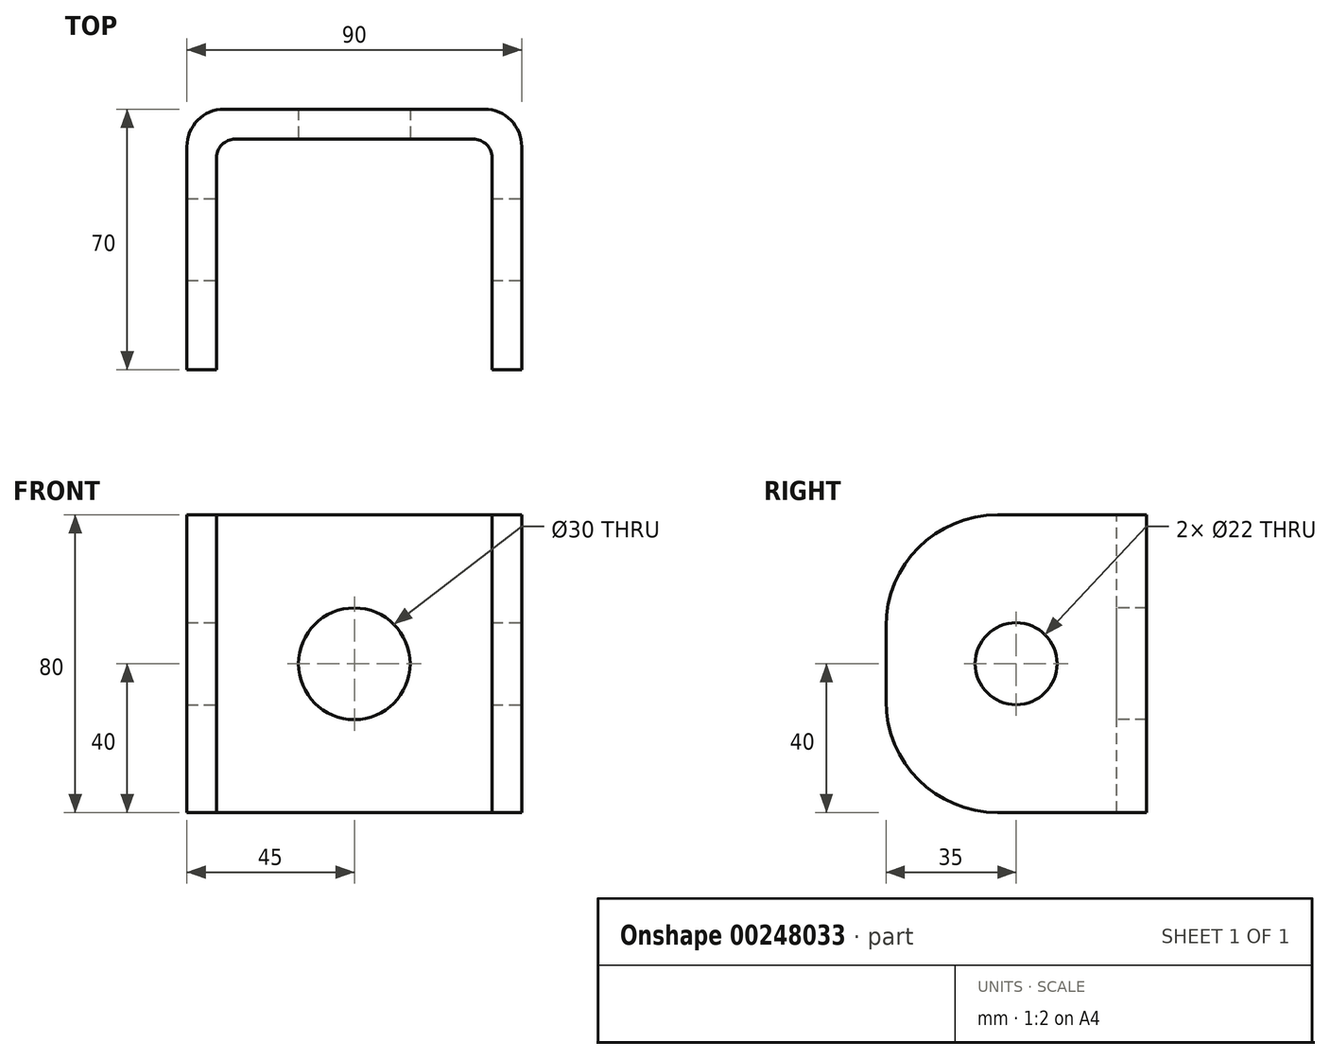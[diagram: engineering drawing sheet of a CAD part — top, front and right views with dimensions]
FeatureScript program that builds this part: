
annotation { "Feature Type Name" : "Feature", "Feature Type Description" : "" }
export const myFeature = defineFeature(function(context is Context, id is Id, definition is map)
    precondition{}
    {
        {
            var Q0;
            Q0=qCreatedBy(makeId("Front.planeOp"),FACE);
            var sketch = newSketch(context, id + "F0", { "sketchPlane" : qUnion([Q0])});
            skLineSegment(sketch, "E0.bottom", {"start": v(45, -40) * mm, "end": v(-45, -40) * mm});
            skLineSegment(sketch, "E0.top", {"start": v(45, 40) * mm, "end": v(-45, 40) * mm});
            skLineSegment(sketch, "E0.left", {"start": v(45, -40) * mm, "end": v(45, 40) * mm});
            skLineSegment(sketch, "E0.right", {"start": v(-45, -40) * mm, "end": v(-45, 40) * mm});
            skPoint(sketch, "E0.middle", {"position": v(0, 0) * mm});
            skSolve(sketch);
        }
        {
            var Q0;
            Q0=makeQuery(id+"F0.imprint","IMPRINT",FACE,{"disambiguationData":[TD([[makeQuery(id+"F0.imprint","IMPRINT",EDGE,{"derivedFrom":sQuery(id+"F0.wireOp",EDGE,"E0.bottom")}),-1.0]])]});
            extrude(context, id + "F1", {"entities" : qUnion([Q0]), "depth" : 70 * mm});
        }
        {
            var Q0;
            Q0=makeQuery(id+"F1.opExtrude","CAP_FACE",FACE,{"disambiguationData":[OSD([sQuery(id+"F0.wireOp",EDGE,"E0.bottom"),sQuery(id+"F0.wireOp",EDGE,"E0.top"),sQuery(id+"F0.wireOp",EDGE,"E0.left"),sQuery(id+"F0.wireOp",EDGE,"E0.right")])],"isStart":false});
            var Q1;
            Q1=makeQuery(id+"F1.opExtrude","SWEPT_FACE",FACE,{"disambiguationData":[OSD([sQuery(id+"F0.wireOp",EDGE,"E0.top")])]});
            var Q2;
            Q2=makeQuery(id+"F1.opExtrude","SWEPT_FACE",FACE,{"disambiguationData":[OSD([sQuery(id+"F0.wireOp",EDGE,"E0.bottom")])]});
            shell(context, id + "F2", {"entities" : qUnion([Q0, Q1, Q2]), "thickness" : 8 * mm});
        }
        {
            var Q0;
            {var subQ0=sQuery(id+"F0.wireOp",EDGE,"E0.right");Q0=makeQuery(id+"F2.opShell","OFFSET_EDGE",EDGE,{"disambiguationData":[OSD([subQ0]),TDD([makeQuery(id+"F1.opExtrude","CAP_EDGE",EDGE,{"disambiguationData":[OSD([subQ0])],"isStart":true})])]});}
            var Q1;
            {var subQ0=sQuery(id+"F0.wireOp",EDGE,"E0.left");Q1=makeQuery(id+"F2.opShell","OFFSET_EDGE",EDGE,{"disambiguationData":[OSD([subQ0]),TDD([makeQuery(id+"F1.opExtrude","CAP_EDGE",EDGE,{"disambiguationData":[OSD([subQ0])],"isStart":true})])]});}
            fillet(context, id + "F3", {"entities" : qUnion([Q0, Q1]), "radius" : 5 * mm, "tangentPropagation" : true, "allowEdgeOverflow" : false});
        }
        {
            var Q0;
            Q0=makeQuery(id+"F1.opExtrude","CAP_EDGE",EDGE,{"disambiguationData":[OSD([sQuery(id+"F0.wireOp",EDGE,"E0.right")])],"isStart":true});
            var Q1;
            Q1=makeQuery(id+"F1.opExtrude","CAP_EDGE",EDGE,{"disambiguationData":[OSD([sQuery(id+"F0.wireOp",EDGE,"E0.left")])],"isStart":true});
            fillet(context, id + "F4", {"entities" : qUnion([Q0, Q1]), "radius" : 10 * mm, "tangentPropagation" : true, "allowEdgeOverflow" : false});
        }
        {
            var Q0;
            {var subQ0=sQuery(id+"F0.wireOp",EDGE,"E0.bottom");Q0=makeQuery(id+"F2.opShell","OFFSET_EDGE",EDGE,{"disambiguationData":[OSD([subQ0]),TDD([makeQuery(id+"F1.opExtrude","CAP_EDGE",EDGE,{"disambiguationData":[OSD([subQ0])],"isStart":false})])]});}
            var Q1;
            {var subQ0=sQuery(id+"F0.wireOp",EDGE,"E0.top");Q1=makeQuery(id+"F2.opShell","OFFSET_EDGE",EDGE,{"disambiguationData":[OSD([subQ0]),TDD([makeQuery(id+"F1.opExtrude","CAP_EDGE",EDGE,{"disambiguationData":[OSD([subQ0])],"isStart":false})])]});}
            var Q2;
            Q2=makeQuery(id+"F1.opExtrude","CAP_EDGE",EDGE,{"disambiguationData":[OSD([sQuery(id+"F0.wireOp",EDGE,"E0.top")])],"isStart":false});
            var Q3;
            Q3=makeQuery(id+"F1.opExtrude","CAP_EDGE",EDGE,{"disambiguationData":[OSD([sQuery(id+"F0.wireOp",EDGE,"E0.bottom")])],"isStart":false});
            fillet(context, id + "F5", {"entities" : qUnion([Q0, Q1, Q2, Q3]), "radius" : 30 * mm, "tangentPropagation" : true, "allowEdgeOverflow" : false});
        }
        {
            var Q0;
            {var subQ0=sQuery(id+"F0.wireOp",EDGE,"E0.right");var subQ1=sQuery(id+"F0.wireOp",EDGE,"E0.left");var subQ2=sQuery(id+"F0.wireOp",EDGE,"E0.top");var subQ3=sQuery(id+"F0.wireOp",EDGE,"E0.bottom");Q0=makeQuery(id+"F2.opShell","OFFSET_FACE",FACE,{"disambiguationData":[OSD([subQ3,subQ2,subQ1,subQ0]),TDD([makeQuery(id+"F1.opExtrude","CAP_FACE",FACE,{"disambiguationData":[OSD([subQ3,subQ2,subQ1,subQ0])],"isStart":true})])]});}
            var sketch = newSketch(context, id + "F6", { "sketchPlane" : qUnion([Q0])});
            skPoint(sketch, "E1", {"position": v(0, 0) * mm});
            skSolve(sketch);
        }
        {
            var Q0;
            Q0=sQuery(id+"F6.wireOp",VERTEX,"E1");
            var Q1;
            Q1=makeQuery(id+"F1.opExtrude","SWEPT_BODY",BODY,{"disambiguationData":[OSD([sQuery(id+"F0.wireOp",EDGE,"E0.bottom"),sQuery(id+"F0.wireOp",EDGE,"E0.top"),sQuery(id+"F0.wireOp",EDGE,"E0.left"),sQuery(id+"F0.wireOp",EDGE,"E0.right")])]});
            hole(context, id + "F7", {"style" : HoleStyle.SIMPLE, "endStyle" : HoleEndStyle.THROUGH, "holeDiameter" : 30 * mm, "tappedDepth" : 12 * mm, "tapClearance" : 3, "locations" : qUnion([Q0]), "scope" : qUnion([Q1])});
        }
        {
            var Q0;
            Q0=makeQuery(id+"F1.opExtrude","SWEPT_FACE",FACE,{"disambiguationData":[OSD([sQuery(id+"F0.wireOp",EDGE,"E0.left")])]});
            var sketch = newSketch(context, id + "F8", { "sketchPlane" : qUnion([Q0])});
            skPoint(sketch, "E2", {"position": v(-35, 0) * mm});
            skPoint(sketch, "E2.positionSnap0", {"position": v(-70, 0) * mm});
            skSolve(sketch);
        }
        {
            var Q0;
            Q0=sQuery(id+"F8.wireOp",VERTEX,"E2");
            var Q1;
            Q1=makeQuery(id+"F1.opExtrude","SWEPT_BODY",BODY,{"disambiguationData":[OSD([sQuery(id+"F0.wireOp",EDGE,"E0.bottom"),sQuery(id+"F0.wireOp",EDGE,"E0.top"),sQuery(id+"F0.wireOp",EDGE,"E0.left"),sQuery(id+"F0.wireOp",EDGE,"E0.right")])]});
            hole(context, id + "F9", {"style" : HoleStyle.SIMPLE, "endStyle" : HoleEndStyle.THROUGH, "holeDiameter" : 22 * mm, "tappedDepth" : 12 * mm, "tapClearance" : 3, "locations" : qUnion([Q0]), "scope" : qUnion([Q1])});
        }
    });
